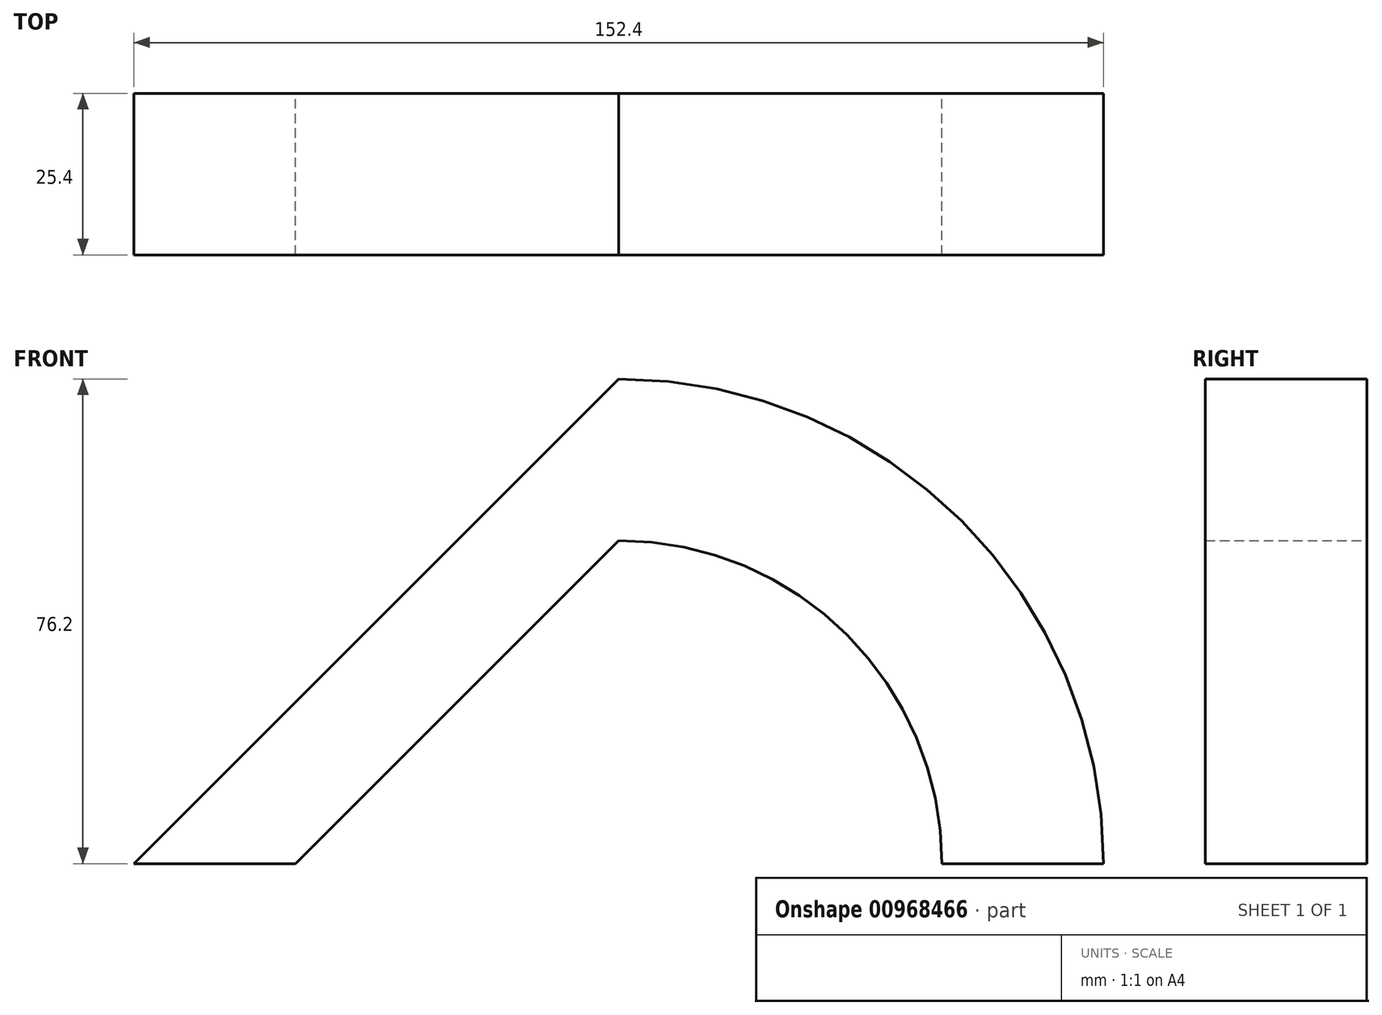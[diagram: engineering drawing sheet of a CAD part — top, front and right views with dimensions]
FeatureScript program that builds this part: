
annotation { "Feature Type Name" : "Feature", "Feature Type Description" : "" }
export const myFeature = defineFeature(function(context is Context, id is Id, definition is map)
    precondition{}
    {
        {
            var Q0;
            Q0=qCreatedBy(makeId("Front.planeOp"),FACE);
            var sketch = newSketch(context, id + "F0", { "sketchPlane" : qUnion([Q0])});
            skLineSegment(sketch, "E0", {"start": v(0, 50.8) * mm, "end": v(-50.8, 0) * mm});
            skLineSegment(sketch, "E1", {"start": v(-50.8, 0) * mm, "end": v(-76.2, 0) * mm});
            skLineSegment(sketch, "E2", {"start": v(-76.2, 0) * mm, "end": v(0, 76.2) * mm});
            skLineSegment(sketch, "E3", {"start": v(0, 76.2) * mm, "end": v(0, 50.8) * mm});
            skArc(sketch, "E4", {"start": v(50.8, 0) * mm, "mid": v(35.92, 35.92) * mm, "end": v(0, 50.8) * mm});
            skLineSegment(sketch, "E5", {"start": v(50.8, 0) * mm, "end": v(76.2, 0) * mm});
            skArc(sketch, "E6", {"start": v(76.2, 0) * mm, "mid": v(53.88, 53.88) * mm, "end": v(0, 76.2) * mm});
            skSolve(sketch);
        }
        {
            var Q0;
            Q0 = qSketchRegion(id + "F0", true);
            extrude(context, id + "F1", {"entities" : qUnion([Q0]), "depth" : 25.4 * mm, "offsetDistance" : 25.4 * mm});
        }
    });
